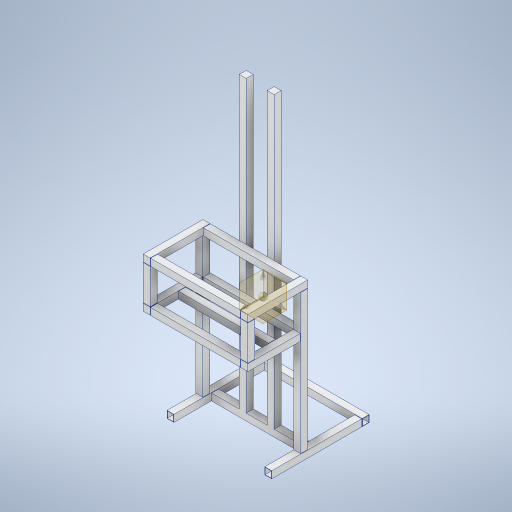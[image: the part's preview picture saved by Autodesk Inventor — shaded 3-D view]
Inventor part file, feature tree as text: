
AUTODESK INVENTOR PART (.ipt)
format: ipt  version: 2023 (Build 270158000, 158)  size: 548,864 bytes
history: native  units: mm
features: extrude x13, other x12, sketch x7
ambient origin geometry x8: Origin, YZ Plane, XZ Plane, XY Plane, X Axis, Y Axis, Z Axis, Center Point
bodies: Body1 (feature_tree)
feature tree (32):
  other  "Твердое тело1"
  other  "РабПлоскость2"
  other  "РабПлоскость6"
  extrude  "Выдавливание10"  Depth=600.0mm
  extrude  "Выдавливание20"  Depth=300.0mm
  other  "РабПлоскость16"
  extrude  "Выдавливание21"  Depth=40.0mm
  extrude  "Выдавливание25"  Depth=2.0mm
  other  "РабПлоскость12"
  extrude  "Выдавливание26"  Depth=40.0mm
  other  "РабПлоскость22"
  other  "РабПлоскость15"
  extrude  "Выдавливание28"  Depth=40.0mm
  other  "РабПлоскость18"
  other  "РабПлоскость21"
  extrude  "Выдавливание36"  Depth=300.0mm
  extrude  "Выдавливание37"  Depth=2.0mm
  other  "РабПлоскость23"
  extrude  "Выдавливание38"  Depth=216.0mm
  other  "РабПлоскость24"
  extrude  "Выдавливание39"  Depth=40.0mm TaperAngle=0.0deg
  other  "РабПлоскость25"
  extrude  "Выдавливание40"  Depth=100.0mm
  extrude  "Выдавливание41"  Depth=2.0mm
  extrude  "Выдавливание42"  Depth=200.0mm
  sketch  "Эскиз30"
  sketch  "Эскиз41"
  sketch  "Эскиз42"
  sketch  "Эскиз43"
  sketch  "Эскиз44"
  sketch  "Эскиз45"
  sketch  "Эскиз46"
